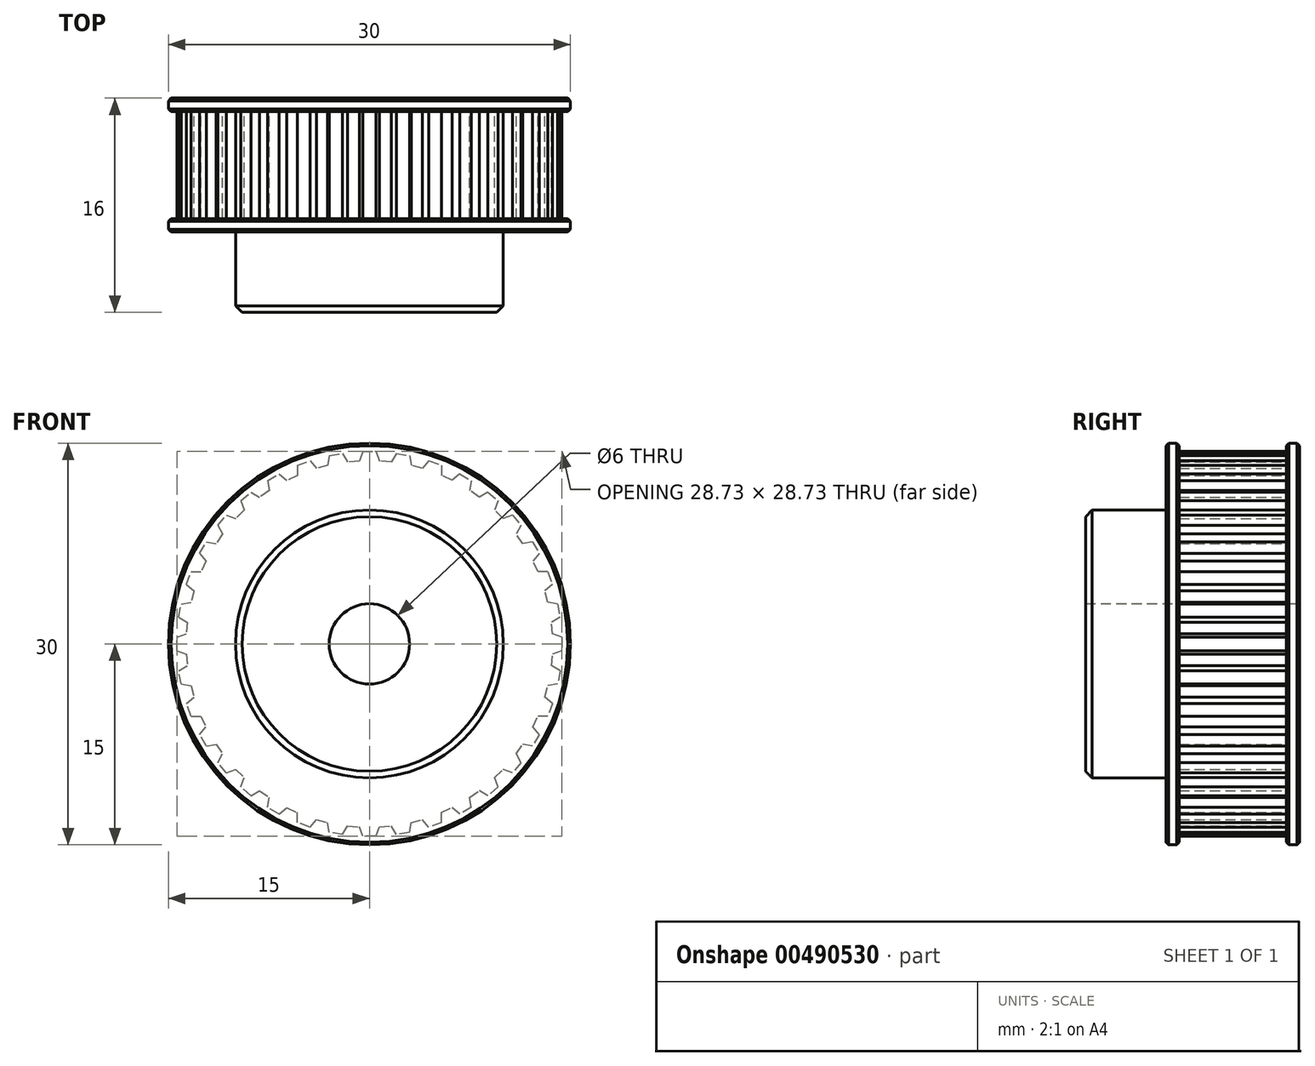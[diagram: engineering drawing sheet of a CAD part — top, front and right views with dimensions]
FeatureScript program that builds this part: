
annotation { "Feature Type Name" : "Feature", "Feature Type Description" : "" }
export const myFeature = defineFeature(function(context is Context, id is Id, definition is map)
    precondition{}
    {
        {
            var Q0;
            Q0=qCreatedBy(makeId("Front.planeOp"),FACE);
            var sketch = newSketch(context, id + "F0", { "sketchPlane" : qUnion([Q0])});
            skCircle(sketch, "E0", {"center": v(0, 0) * mm, "radius": 14.38 * mm, "construction": true});
            skCircle(sketch, "E1", {"center": v(0, 0) * mm, "radius": 10 * mm});
            skLineSegment(sketch, "E2", {"start": v(0, 14.37) * mm, "end": v(-0.5, 14.37) * mm});
            skLineSegment(sketch, "E3", {"start": v(-0.5, 14.37) * mm, "end": v(-0.75, 13.67) * mm});
            skLineSegment(sketch, "E4", {"start": v(-0.75, 13.67) * mm, "end": v(0, 13.67) * mm});
            skLineSegment(sketch, "E5.MirrorCS", {"start": v(0.75, 13.67) * mm, "end": v(0, 13.67) * mm});
            skLineSegment(sketch, "E6.MirrorCS", {"start": v(0, 14.37) * mm, "end": v(0.5, 14.37) * mm});
            skLineSegment(sketch, "E7.MirrorCS", {"start": v(0.5, 14.37) * mm, "end": v(0.75, 13.67) * mm});
            skLineSegment(sketch, "E8.1.0", {"start": v(1.63, 13.59) * mm, "end": v(2.37, 13.46) * mm});
            skLineSegment(sketch, "E8.1.1", {"start": v(3.12, 13.33) * mm, "end": v(2.37, 13.46) * mm});
            skLineSegment(sketch, "E8.1.2", {"start": v(2.99, 14.06) * mm, "end": v(3.12, 13.33) * mm});
            skLineSegment(sketch, "E8.1.3", {"start": v(2, 14.23) * mm, "end": v(1.63, 13.59) * mm});
            skLineSegment(sketch, "E8.1.4", {"start": v(2.5, 14.15) * mm, "end": v(2.99, 14.06) * mm});
            skLineSegment(sketch, "E8.1.5", {"start": v(2.5, 14.15) * mm, "end": v(2, 14.23) * mm});
            skLineSegment(sketch, "E8.2.0", {"start": v(3.96, 13.1) * mm, "end": v(4.67, 12.84) * mm});
            skLineSegment(sketch, "E8.2.1", {"start": v(5.38, 12.58) * mm, "end": v(4.67, 12.84) * mm});
            skLineSegment(sketch, "E8.2.2", {"start": v(5.38, 13.33) * mm, "end": v(5.38, 12.58) * mm});
            skLineSegment(sketch, "E8.2.3", {"start": v(4.44, 13.67) * mm, "end": v(3.96, 13.1) * mm});
            skLineSegment(sketch, "E8.2.4", {"start": v(4.91, 13.5) * mm, "end": v(5.38, 13.33) * mm});
            skLineSegment(sketch, "E8.2.5", {"start": v(4.91, 13.5) * mm, "end": v(4.44, 13.67) * mm});
            skLineSegment(sketch, "E8.3.0", {"start": v(6.18, 12.21) * mm, "end": v(6.83, 11.84) * mm});
            skLineSegment(sketch, "E8.3.1", {"start": v(7.49, 11.46) * mm, "end": v(6.83, 11.84) * mm});
            skLineSegment(sketch, "E8.3.2", {"start": v(7.62, 12.2) * mm, "end": v(7.49, 11.46) * mm});
            skLineSegment(sketch, "E8.3.3", {"start": v(6.75, 12.7) * mm, "end": v(6.18, 12.21) * mm});
            skLineSegment(sketch, "E8.3.4", {"start": v(7.18, 12.44) * mm, "end": v(7.62, 12.2) * mm});
            skLineSegment(sketch, "E8.3.5", {"start": v(7.18, 12.44) * mm, "end": v(6.75, 12.7) * mm});
            skLineSegment(sketch, "E8.4.0", {"start": v(8.2, 10.95) * mm, "end": v(8.78, 10.47) * mm});
            skLineSegment(sketch, "E8.4.1", {"start": v(9.36, 9.98) * mm, "end": v(8.78, 10.47) * mm});
            skLineSegment(sketch, "E8.4.2", {"start": v(9.62, 10.68) * mm, "end": v(9.36, 9.98) * mm});
            skLineSegment(sketch, "E8.4.3", {"start": v(8.85, 11.33) * mm, "end": v(8.2, 10.95) * mm});
            skLineSegment(sketch, "E8.4.4", {"start": v(9.23, 11) * mm, "end": v(9.62, 10.68) * mm});
            skLineSegment(sketch, "E8.4.5", {"start": v(9.23, 11) * mm, "end": v(8.85, 11.33) * mm});
            skLineSegment(sketch, "E8.5.0", {"start": v(9.98, 9.36) * mm, "end": v(10.47, 8.78) * mm});
            skLineSegment(sketch, "E8.5.1", {"start": v(10.95, 8.2) * mm, "end": v(10.47, 8.78) * mm});
            skLineSegment(sketch, "E8.5.2", {"start": v(11.33, 8.85) * mm, "end": v(10.95, 8.2) * mm});
            skLineSegment(sketch, "E8.5.3", {"start": v(10.68, 9.62) * mm, "end": v(9.98, 9.36) * mm});
            skLineSegment(sketch, "E8.5.4", {"start": v(11, 9.23) * mm, "end": v(11.33, 8.85) * mm});
            skLineSegment(sketch, "E8.5.5", {"start": v(11, 9.23) * mm, "end": v(10.68, 9.62) * mm});
            skLineSegment(sketch, "E8.6.0", {"start": v(11.46, 7.49) * mm, "end": v(11.84, 6.83) * mm});
            skLineSegment(sketch, "E8.6.1", {"start": v(12.21, 6.18) * mm, "end": v(11.84, 6.83) * mm});
            skLineSegment(sketch, "E8.6.2", {"start": v(12.7, 6.75) * mm, "end": v(12.21, 6.18) * mm});
            skLineSegment(sketch, "E8.6.3", {"start": v(12.2, 7.62) * mm, "end": v(11.46, 7.49) * mm});
            skLineSegment(sketch, "E8.6.4", {"start": v(12.44, 7.18) * mm, "end": v(12.7, 6.75) * mm});
            skLineSegment(sketch, "E8.6.5", {"start": v(12.44, 7.18) * mm, "end": v(12.2, 7.62) * mm});
            skLineSegment(sketch, "E8.7.0", {"start": v(12.58, 5.38) * mm, "end": v(12.84, 4.67) * mm});
            skLineSegment(sketch, "E8.7.1", {"start": v(13.1, 3.96) * mm, "end": v(12.84, 4.67) * mm});
            skLineSegment(sketch, "E8.7.2", {"start": v(13.67, 4.44) * mm, "end": v(13.1, 3.96) * mm});
            skLineSegment(sketch, "E8.7.3", {"start": v(13.33, 5.38) * mm, "end": v(12.58, 5.38) * mm});
            skLineSegment(sketch, "E8.7.4", {"start": v(13.5, 4.91) * mm, "end": v(13.67, 4.44) * mm});
            skLineSegment(sketch, "E8.7.5", {"start": v(13.5, 4.91) * mm, "end": v(13.33, 5.38) * mm});
            skLineSegment(sketch, "E8.8.0", {"start": v(13.33, 3.12) * mm, "end": v(13.46, 2.37) * mm});
            skLineSegment(sketch, "E8.8.1", {"start": v(13.59, 1.63) * mm, "end": v(13.46, 2.37) * mm});
            skLineSegment(sketch, "E8.8.2", {"start": v(14.23, 2) * mm, "end": v(13.59, 1.63) * mm});
            skLineSegment(sketch, "E8.8.3", {"start": v(14.06, 2.99) * mm, "end": v(13.33, 3.12) * mm});
            skLineSegment(sketch, "E8.8.4", {"start": v(14.15, 2.5) * mm, "end": v(14.23, 2) * mm});
            skLineSegment(sketch, "E8.8.5", {"start": v(14.15, 2.5) * mm, "end": v(14.06, 2.99) * mm});
            skLineSegment(sketch, "E8.9.0", {"start": v(13.67, 0.75) * mm, "end": v(13.67, 0) * mm});
            skLineSegment(sketch, "E8.9.1", {"start": v(13.67, -0.75) * mm, "end": v(13.67, 0) * mm});
            skLineSegment(sketch, "E8.9.2", {"start": v(14.37, -0.5) * mm, "end": v(13.67, -0.75) * mm});
            skLineSegment(sketch, "E8.9.3", {"start": v(14.37, 0.5) * mm, "end": v(13.67, 0.75) * mm});
            skLineSegment(sketch, "E8.9.4", {"start": v(14.37, 0) * mm, "end": v(14.37, -0.5) * mm});
            skLineSegment(sketch, "E8.9.5", {"start": v(14.37, 0) * mm, "end": v(14.37, 0.5) * mm});
            skLineSegment(sketch, "E8.10.0", {"start": v(13.59, -1.63) * mm, "end": v(13.46, -2.37) * mm});
            skLineSegment(sketch, "E8.10.1", {"start": v(13.33, -3.12) * mm, "end": v(13.46, -2.37) * mm});
            skLineSegment(sketch, "E8.10.2", {"start": v(14.06, -2.99) * mm, "end": v(13.33, -3.12) * mm});
            skLineSegment(sketch, "E8.10.3", {"start": v(14.23, -2) * mm, "end": v(13.59, -1.63) * mm});
            skLineSegment(sketch, "E8.10.4", {"start": v(14.15, -2.5) * mm, "end": v(14.06, -2.99) * mm});
            skLineSegment(sketch, "E8.10.5", {"start": v(14.15, -2.5) * mm, "end": v(14.23, -2) * mm});
            skLineSegment(sketch, "E8.11.0", {"start": v(13.1, -3.96) * mm, "end": v(12.84, -4.67) * mm});
            skLineSegment(sketch, "E8.11.1", {"start": v(12.58, -5.38) * mm, "end": v(12.84, -4.67) * mm});
            skLineSegment(sketch, "E8.11.2", {"start": v(13.33, -5.38) * mm, "end": v(12.58, -5.38) * mm});
            skLineSegment(sketch, "E8.11.3", {"start": v(13.67, -4.44) * mm, "end": v(13.1, -3.96) * mm});
            skLineSegment(sketch, "E8.11.4", {"start": v(13.5, -4.91) * mm, "end": v(13.33, -5.38) * mm});
            skLineSegment(sketch, "E8.11.5", {"start": v(13.5, -4.91) * mm, "end": v(13.67, -4.44) * mm});
            skLineSegment(sketch, "E8.12.0", {"start": v(12.21, -6.18) * mm, "end": v(11.84, -6.83) * mm});
            skLineSegment(sketch, "E8.12.1", {"start": v(11.46, -7.49) * mm, "end": v(11.84, -6.83) * mm});
            skLineSegment(sketch, "E8.12.2", {"start": v(12.2, -7.62) * mm, "end": v(11.46, -7.49) * mm});
            skLineSegment(sketch, "E8.12.3", {"start": v(12.7, -6.75) * mm, "end": v(12.21, -6.18) * mm});
            skLineSegment(sketch, "E8.12.4", {"start": v(12.44, -7.18) * mm, "end": v(12.2, -7.62) * mm});
            skLineSegment(sketch, "E8.12.5", {"start": v(12.44, -7.18) * mm, "end": v(12.7, -6.75) * mm});
            skLineSegment(sketch, "E8.13.0", {"start": v(10.95, -8.2) * mm, "end": v(10.47, -8.78) * mm});
            skLineSegment(sketch, "E8.13.1", {"start": v(9.98, -9.36) * mm, "end": v(10.47, -8.78) * mm});
            skLineSegment(sketch, "E8.13.2", {"start": v(10.68, -9.62) * mm, "end": v(9.98, -9.36) * mm});
            skLineSegment(sketch, "E8.13.3", {"start": v(11.33, -8.85) * mm, "end": v(10.95, -8.2) * mm});
            skLineSegment(sketch, "E8.13.4", {"start": v(11, -9.23) * mm, "end": v(10.68, -9.62) * mm});
            skLineSegment(sketch, "E8.13.5", {"start": v(11, -9.23) * mm, "end": v(11.33, -8.85) * mm});
            skLineSegment(sketch, "E8.14.0", {"start": v(9.36, -9.98) * mm, "end": v(8.78, -10.47) * mm});
            skLineSegment(sketch, "E8.14.1", {"start": v(8.2, -10.95) * mm, "end": v(8.78, -10.47) * mm});
            skLineSegment(sketch, "E8.14.2", {"start": v(8.85, -11.33) * mm, "end": v(8.2, -10.95) * mm});
            skLineSegment(sketch, "E8.14.3", {"start": v(9.62, -10.68) * mm, "end": v(9.36, -9.98) * mm});
            skLineSegment(sketch, "E8.14.4", {"start": v(9.23, -11) * mm, "end": v(8.85, -11.33) * mm});
            skLineSegment(sketch, "E8.14.5", {"start": v(9.23, -11) * mm, "end": v(9.62, -10.68) * mm});
            skLineSegment(sketch, "E8.15.0", {"start": v(7.49, -11.46) * mm, "end": v(6.83, -11.84) * mm});
            skLineSegment(sketch, "E8.15.1", {"start": v(6.18, -12.21) * mm, "end": v(6.83, -11.84) * mm});
            skLineSegment(sketch, "E8.15.2", {"start": v(6.75, -12.7) * mm, "end": v(6.18, -12.21) * mm});
            skLineSegment(sketch, "E8.15.3", {"start": v(7.62, -12.2) * mm, "end": v(7.49, -11.46) * mm});
            skLineSegment(sketch, "E8.15.4", {"start": v(7.18, -12.44) * mm, "end": v(6.75, -12.7) * mm});
            skLineSegment(sketch, "E8.15.5", {"start": v(7.18, -12.44) * mm, "end": v(7.62, -12.2) * mm});
            skLineSegment(sketch, "E8.16.0", {"start": v(5.38, -12.58) * mm, "end": v(4.67, -12.84) * mm});
            skLineSegment(sketch, "E8.16.1", {"start": v(3.96, -13.1) * mm, "end": v(4.67, -12.84) * mm});
            skLineSegment(sketch, "E8.16.2", {"start": v(4.44, -13.67) * mm, "end": v(3.96, -13.1) * mm});
            skLineSegment(sketch, "E8.16.3", {"start": v(5.38, -13.33) * mm, "end": v(5.38, -12.58) * mm});
            skLineSegment(sketch, "E8.16.4", {"start": v(4.91, -13.5) * mm, "end": v(4.44, -13.67) * mm});
            skLineSegment(sketch, "E8.16.5", {"start": v(4.91, -13.5) * mm, "end": v(5.38, -13.33) * mm});
            skLineSegment(sketch, "E8.17.0", {"start": v(3.12, -13.33) * mm, "end": v(2.37, -13.46) * mm});
            skLineSegment(sketch, "E8.17.1", {"start": v(1.63, -13.59) * mm, "end": v(2.37, -13.46) * mm});
            skLineSegment(sketch, "E8.17.2", {"start": v(2, -14.23) * mm, "end": v(1.63, -13.59) * mm});
            skLineSegment(sketch, "E8.17.3", {"start": v(2.99, -14.06) * mm, "end": v(3.12, -13.33) * mm});
            skLineSegment(sketch, "E8.17.4", {"start": v(2.5, -14.15) * mm, "end": v(2, -14.23) * mm});
            skLineSegment(sketch, "E8.17.5", {"start": v(2.5, -14.15) * mm, "end": v(2.99, -14.06) * mm});
            skLineSegment(sketch, "E8.18.0", {"start": v(0.75, -13.67) * mm, "end": v(0, -13.67) * mm});
            skLineSegment(sketch, "E8.18.1", {"start": v(-0.75, -13.67) * mm, "end": v(0, -13.67) * mm});
            skLineSegment(sketch, "E8.18.2", {"start": v(-0.5, -14.37) * mm, "end": v(-0.75, -13.67) * mm});
            skLineSegment(sketch, "E8.18.3", {"start": v(0.5, -14.37) * mm, "end": v(0.75, -13.67) * mm});
            skLineSegment(sketch, "E8.18.4", {"start": v(0, -14.37) * mm, "end": v(-0.5, -14.37) * mm});
            skLineSegment(sketch, "E8.18.5", {"start": v(0, -14.37) * mm, "end": v(0.5, -14.37) * mm});
            skLineSegment(sketch, "E8.19.0", {"start": v(-1.63, -13.59) * mm, "end": v(-2.37, -13.46) * mm});
            skLineSegment(sketch, "E8.19.1", {"start": v(-3.12, -13.33) * mm, "end": v(-2.37, -13.46) * mm});
            skLineSegment(sketch, "E8.19.2", {"start": v(-2.99, -14.06) * mm, "end": v(-3.12, -13.33) * mm});
            skLineSegment(sketch, "E8.19.3", {"start": v(-2, -14.23) * mm, "end": v(-1.63, -13.59) * mm});
            skLineSegment(sketch, "E8.19.4", {"start": v(-2.5, -14.15) * mm, "end": v(-2.99, -14.06) * mm});
            skLineSegment(sketch, "E8.19.5", {"start": v(-2.5, -14.15) * mm, "end": v(-2, -14.23) * mm});
            skLineSegment(sketch, "E8.20.0", {"start": v(-3.96, -13.1) * mm, "end": v(-4.67, -12.84) * mm});
            skLineSegment(sketch, "E8.20.1", {"start": v(-5.38, -12.58) * mm, "end": v(-4.67, -12.84) * mm});
            skLineSegment(sketch, "E8.20.2", {"start": v(-5.38, -13.33) * mm, "end": v(-5.38, -12.58) * mm});
            skLineSegment(sketch, "E8.20.3", {"start": v(-4.44, -13.67) * mm, "end": v(-3.96, -13.1) * mm});
            skLineSegment(sketch, "E8.20.4", {"start": v(-4.91, -13.5) * mm, "end": v(-5.38, -13.33) * mm});
            skLineSegment(sketch, "E8.20.5", {"start": v(-4.91, -13.5) * mm, "end": v(-4.44, -13.67) * mm});
            skLineSegment(sketch, "E8.21.0", {"start": v(-6.18, -12.21) * mm, "end": v(-6.83, -11.84) * mm});
            skLineSegment(sketch, "E8.21.1", {"start": v(-7.49, -11.46) * mm, "end": v(-6.83, -11.84) * mm});
            skLineSegment(sketch, "E8.21.2", {"start": v(-7.62, -12.2) * mm, "end": v(-7.49, -11.46) * mm});
            skLineSegment(sketch, "E8.21.3", {"start": v(-6.75, -12.7) * mm, "end": v(-6.18, -12.21) * mm});
            skLineSegment(sketch, "E8.21.4", {"start": v(-7.18, -12.44) * mm, "end": v(-7.62, -12.2) * mm});
            skLineSegment(sketch, "E8.21.5", {"start": v(-7.18, -12.44) * mm, "end": v(-6.75, -12.7) * mm});
            skLineSegment(sketch, "E8.22.0", {"start": v(-8.2, -10.95) * mm, "end": v(-8.78, -10.47) * mm});
            skLineSegment(sketch, "E8.22.1", {"start": v(-9.36, -9.98) * mm, "end": v(-8.78, -10.47) * mm});
            skLineSegment(sketch, "E8.22.2", {"start": v(-9.62, -10.68) * mm, "end": v(-9.36, -9.98) * mm});
            skLineSegment(sketch, "E8.22.3", {"start": v(-8.85, -11.33) * mm, "end": v(-8.2, -10.95) * mm});
            skLineSegment(sketch, "E8.22.4", {"start": v(-9.23, -11) * mm, "end": v(-9.62, -10.68) * mm});
            skLineSegment(sketch, "E8.22.5", {"start": v(-9.23, -11) * mm, "end": v(-8.85, -11.33) * mm});
            skLineSegment(sketch, "E8.23.0", {"start": v(-9.98, -9.36) * mm, "end": v(-10.47, -8.78) * mm});
            skLineSegment(sketch, "E8.23.1", {"start": v(-10.95, -8.2) * mm, "end": v(-10.47, -8.78) * mm});
            skLineSegment(sketch, "E8.23.2", {"start": v(-11.33, -8.85) * mm, "end": v(-10.95, -8.2) * mm});
            skLineSegment(sketch, "E8.23.3", {"start": v(-10.68, -9.62) * mm, "end": v(-9.98, -9.36) * mm});
            skLineSegment(sketch, "E8.23.4", {"start": v(-11, -9.23) * mm, "end": v(-11.33, -8.85) * mm});
            skLineSegment(sketch, "E8.23.5", {"start": v(-11, -9.23) * mm, "end": v(-10.68, -9.62) * mm});
            skLineSegment(sketch, "E8.anchor1", {"start": v(0, 0) * mm, "end": v(-0.75, 13.67) * mm, "construction": true});
            skLineSegment(sketch, "E8.anchor2", {"start": v(0, 0) * mm, "end": v(-3.12, 13.33) * mm, "construction": true});
            skLineSegment(sketch, "E9", {"start": v(-0.75, 13.67) * mm, "end": v(-1.63, 13.59) * mm});
            skLineSegment(sketch, "E10.1.0", {"start": v(1.63, 13.59) * mm, "end": v(0.75, 13.67) * mm});
            skLineSegment(sketch, "E10.2.0", {"start": v(3.96, 13.1) * mm, "end": v(3.12, 13.33) * mm});
            skLineSegment(sketch, "E10.3.0", {"start": v(6.18, 12.21) * mm, "end": v(5.38, 12.58) * mm});
            skLineSegment(sketch, "E10.4.0", {"start": v(8.2, 10.95) * mm, "end": v(7.49, 11.46) * mm});
            skLineSegment(sketch, "E10.5.0", {"start": v(9.98, 9.36) * mm, "end": v(9.36, 9.98) * mm});
            skLineSegment(sketch, "E10.6.0", {"start": v(11.46, 7.49) * mm, "end": v(10.95, 8.2) * mm});
            skLineSegment(sketch, "E10.7.0", {"start": v(12.58, 5.38) * mm, "end": v(12.21, 6.18) * mm});
            skLineSegment(sketch, "E10.8.0", {"start": v(13.33, 3.12) * mm, "end": v(13.1, 3.96) * mm});
            skLineSegment(sketch, "E10.9.0", {"start": v(13.67, 0.75) * mm, "end": v(13.59, 1.63) * mm});
            skLineSegment(sketch, "E10.10.0", {"start": v(13.59, -1.63) * mm, "end": v(13.67, -0.75) * mm});
            skLineSegment(sketch, "E10.11.0", {"start": v(13.1, -3.96) * mm, "end": v(13.33, -3.12) * mm});
            skLineSegment(sketch, "E10.12.0", {"start": v(12.21, -6.18) * mm, "end": v(12.58, -5.38) * mm});
            skLineSegment(sketch, "E10.13.0", {"start": v(10.95, -8.2) * mm, "end": v(11.46, -7.49) * mm});
            skLineSegment(sketch, "E10.14.0", {"start": v(9.36, -9.98) * mm, "end": v(9.98, -9.36) * mm});
            skLineSegment(sketch, "E10.15.0", {"start": v(7.49, -11.46) * mm, "end": v(8.2, -10.95) * mm});
            skLineSegment(sketch, "E10.16.0", {"start": v(5.38, -12.58) * mm, "end": v(6.18, -12.21) * mm});
            skLineSegment(sketch, "E10.17.0", {"start": v(3.12, -13.33) * mm, "end": v(3.96, -13.1) * mm});
            skLineSegment(sketch, "E10.18.0", {"start": v(0.75, -13.67) * mm, "end": v(1.63, -13.59) * mm});
            skLineSegment(sketch, "E10.19.0", {"start": v(-1.63, -13.59) * mm, "end": v(-0.75, -13.67) * mm});
            skLineSegment(sketch, "E10.20.0", {"start": v(-3.96, -13.1) * mm, "end": v(-3.12, -13.33) * mm});
            skLineSegment(sketch, "E10.21.0", {"start": v(-6.18, -12.21) * mm, "end": v(-5.38, -12.58) * mm});
            skLineSegment(sketch, "E10.22.0", {"start": v(-8.2, -10.95) * mm, "end": v(-7.49, -11.46) * mm});
            skLineSegment(sketch, "E10.23.0", {"start": v(-9.98, -9.36) * mm, "end": v(-9.36, -9.98) * mm});
            skLineSegment(sketch, "E10.anchor1", {"start": v(0, 0) * mm, "end": v(-1.63, 13.59) * mm, "construction": true});
            skLineSegment(sketch, "E10.anchor2", {"start": v(0, 0) * mm, "end": v(-3.96, 13.1) * mm, "construction": true});
            skLineSegment(sketch, "E11.2.24.0", {"start": v(-11.46, -7.49) * mm, "end": v(-10.95, -8.2) * mm});
            skLineSegment(sketch, "E11.2.25.0", {"start": v(-12.58, -5.38) * mm, "end": v(-12.21, -6.18) * mm});
            skLineSegment(sketch, "E11.2.26.0", {"start": v(-13.33, -3.12) * mm, "end": v(-13.1, -3.96) * mm});
            skLineSegment(sketch, "E11.2.27.0", {"start": v(-13.67, -0.75) * mm, "end": v(-13.59, -1.63) * mm});
            skLineSegment(sketch, "E11.2.28.0", {"start": v(-13.59, 1.63) * mm, "end": v(-13.67, 0.75) * mm});
            skLineSegment(sketch, "E11.2.29.0", {"start": v(-13.1, 3.96) * mm, "end": v(-13.33, 3.12) * mm});
            skLineSegment(sketch, "E11.2.30.0", {"start": v(-12.21, 6.18) * mm, "end": v(-12.58, 5.38) * mm});
            skLineSegment(sketch, "E11.2.31.0", {"start": v(-10.95, 8.2) * mm, "end": v(-11.46, 7.49) * mm});
            skLineSegment(sketch, "E11.2.32.0", {"start": v(-9.36, 9.98) * mm, "end": v(-9.98, 9.36) * mm});
            skLineSegment(sketch, "E11.2.33.0", {"start": v(-7.49, 11.46) * mm, "end": v(-8.2, 10.95) * mm});
            skLineSegment(sketch, "E11.2.34.0", {"start": v(-5.38, 12.58) * mm, "end": v(-6.18, 12.21) * mm});
            skLineSegment(sketch, "E11.2.35.0", {"start": v(-3.12, 13.33) * mm, "end": v(-3.96, 13.1) * mm});
            skLineSegment(sketch, "E12.1.24.0", {"start": v(-11.46, -7.49) * mm, "end": v(-11.84, -6.83) * mm});
            skLineSegment(sketch, "E12.3.24.0", {"start": v(-12.21, -6.18) * mm, "end": v(-11.84, -6.83) * mm});
            skLineSegment(sketch, "E12.6.24.0", {"start": v(-12.7, -6.75) * mm, "end": v(-12.21, -6.18) * mm});
            skLineSegment(sketch, "E12.9.24.0", {"start": v(-12.2, -7.62) * mm, "end": v(-11.46, -7.49) * mm});
            skLineSegment(sketch, "E12.12.24.0", {"start": v(-12.44, -7.18) * mm, "end": v(-12.7, -6.75) * mm});
            skLineSegment(sketch, "E12.15.24.0", {"start": v(-12.44, -7.18) * mm, "end": v(-12.2, -7.62) * mm});
            skLineSegment(sketch, "E12.1.25.0", {"start": v(-12.58, -5.38) * mm, "end": v(-12.84, -4.67) * mm});
            skLineSegment(sketch, "E12.3.25.0", {"start": v(-13.1, -3.96) * mm, "end": v(-12.84, -4.67) * mm});
            skLineSegment(sketch, "E12.6.25.0", {"start": v(-13.67, -4.44) * mm, "end": v(-13.1, -3.96) * mm});
            skLineSegment(sketch, "E12.9.25.0", {"start": v(-13.33, -5.38) * mm, "end": v(-12.58, -5.38) * mm});
            skLineSegment(sketch, "E12.12.25.0", {"start": v(-13.5, -4.91) * mm, "end": v(-13.67, -4.44) * mm});
            skLineSegment(sketch, "E12.15.25.0", {"start": v(-13.5, -4.91) * mm, "end": v(-13.33, -5.38) * mm});
            skLineSegment(sketch, "E12.1.26.0", {"start": v(-13.33, -3.12) * mm, "end": v(-13.46, -2.37) * mm});
            skLineSegment(sketch, "E12.3.26.0", {"start": v(-13.59, -1.63) * mm, "end": v(-13.46, -2.37) * mm});
            skLineSegment(sketch, "E12.6.26.0", {"start": v(-14.23, -2) * mm, "end": v(-13.59, -1.63) * mm});
            skLineSegment(sketch, "E12.9.26.0", {"start": v(-14.06, -2.99) * mm, "end": v(-13.33, -3.12) * mm});
            skLineSegment(sketch, "E12.12.26.0", {"start": v(-14.15, -2.5) * mm, "end": v(-14.23, -2) * mm});
            skLineSegment(sketch, "E12.15.26.0", {"start": v(-14.15, -2.5) * mm, "end": v(-14.06, -2.99) * mm});
            skLineSegment(sketch, "E12.1.27.0", {"start": v(-13.67, -0.75) * mm, "end": v(-13.67, 0) * mm});
            skLineSegment(sketch, "E12.3.27.0", {"start": v(-13.67, 0.75) * mm, "end": v(-13.67, 0) * mm});
            skLineSegment(sketch, "E12.6.27.0", {"start": v(-14.37, 0.5) * mm, "end": v(-13.67, 0.75) * mm});
            skLineSegment(sketch, "E12.9.27.0", {"start": v(-14.37, -0.5) * mm, "end": v(-13.67, -0.75) * mm});
            skLineSegment(sketch, "E12.12.27.0", {"start": v(-14.37, 0) * mm, "end": v(-14.37, 0.5) * mm});
            skLineSegment(sketch, "E12.15.27.0", {"start": v(-14.37, 0) * mm, "end": v(-14.37, -0.5) * mm});
            skLineSegment(sketch, "E12.1.28.0", {"start": v(-13.59, 1.63) * mm, "end": v(-13.46, 2.37) * mm});
            skLineSegment(sketch, "E12.3.28.0", {"start": v(-13.33, 3.12) * mm, "end": v(-13.46, 2.37) * mm});
            skLineSegment(sketch, "E12.6.28.0", {"start": v(-14.06, 2.99) * mm, "end": v(-13.33, 3.12) * mm});
            skLineSegment(sketch, "E12.9.28.0", {"start": v(-14.23, 2) * mm, "end": v(-13.59, 1.63) * mm});
            skLineSegment(sketch, "E12.12.28.0", {"start": v(-14.15, 2.5) * mm, "end": v(-14.06, 2.99) * mm});
            skLineSegment(sketch, "E12.15.28.0", {"start": v(-14.15, 2.5) * mm, "end": v(-14.23, 2) * mm});
            skLineSegment(sketch, "E12.1.29.0", {"start": v(-13.1, 3.96) * mm, "end": v(-12.84, 4.67) * mm});
            skLineSegment(sketch, "E12.3.29.0", {"start": v(-12.58, 5.38) * mm, "end": v(-12.84, 4.67) * mm});
            skLineSegment(sketch, "E12.6.29.0", {"start": v(-13.33, 5.38) * mm, "end": v(-12.58, 5.38) * mm});
            skLineSegment(sketch, "E12.9.29.0", {"start": v(-13.67, 4.44) * mm, "end": v(-13.1, 3.96) * mm});
            skLineSegment(sketch, "E12.12.29.0", {"start": v(-13.5, 4.91) * mm, "end": v(-13.33, 5.38) * mm});
            skLineSegment(sketch, "E12.15.29.0", {"start": v(-13.5, 4.91) * mm, "end": v(-13.67, 4.44) * mm});
            skLineSegment(sketch, "E12.1.30.0", {"start": v(-12.21, 6.18) * mm, "end": v(-11.84, 6.83) * mm});
            skLineSegment(sketch, "E12.3.30.0", {"start": v(-11.46, 7.49) * mm, "end": v(-11.84, 6.83) * mm});
            skLineSegment(sketch, "E12.6.30.0", {"start": v(-12.2, 7.62) * mm, "end": v(-11.46, 7.49) * mm});
            skLineSegment(sketch, "E12.9.30.0", {"start": v(-12.7, 6.75) * mm, "end": v(-12.21, 6.18) * mm});
            skLineSegment(sketch, "E12.12.30.0", {"start": v(-12.44, 7.18) * mm, "end": v(-12.2, 7.62) * mm});
            skLineSegment(sketch, "E12.15.30.0", {"start": v(-12.44, 7.18) * mm, "end": v(-12.7, 6.75) * mm});
            skLineSegment(sketch, "E12.1.31.0", {"start": v(-10.95, 8.2) * mm, "end": v(-10.47, 8.78) * mm});
            skLineSegment(sketch, "E12.3.31.0", {"start": v(-9.98, 9.36) * mm, "end": v(-10.47, 8.78) * mm});
            skLineSegment(sketch, "E12.6.31.0", {"start": v(-10.68, 9.62) * mm, "end": v(-9.98, 9.36) * mm});
            skLineSegment(sketch, "E12.9.31.0", {"start": v(-11.33, 8.85) * mm, "end": v(-10.95, 8.2) * mm});
            skLineSegment(sketch, "E12.12.31.0", {"start": v(-11, 9.23) * mm, "end": v(-10.68, 9.62) * mm});
            skLineSegment(sketch, "E12.15.31.0", {"start": v(-11, 9.23) * mm, "end": v(-11.33, 8.85) * mm});
            skLineSegment(sketch, "E12.1.32.0", {"start": v(-9.36, 9.98) * mm, "end": v(-8.78, 10.47) * mm});
            skLineSegment(sketch, "E12.3.32.0", {"start": v(-8.2, 10.95) * mm, "end": v(-8.78, 10.47) * mm});
            skLineSegment(sketch, "E12.6.32.0", {"start": v(-8.85, 11.33) * mm, "end": v(-8.2, 10.95) * mm});
            skLineSegment(sketch, "E12.9.32.0", {"start": v(-9.62, 10.68) * mm, "end": v(-9.36, 9.98) * mm});
            skLineSegment(sketch, "E12.12.32.0", {"start": v(-9.23, 11) * mm, "end": v(-8.85, 11.33) * mm});
            skLineSegment(sketch, "E12.15.32.0", {"start": v(-9.23, 11) * mm, "end": v(-9.62, 10.68) * mm});
            skLineSegment(sketch, "E12.1.33.0", {"start": v(-7.49, 11.46) * mm, "end": v(-6.83, 11.84) * mm});
            skLineSegment(sketch, "E12.3.33.0", {"start": v(-6.18, 12.21) * mm, "end": v(-6.83, 11.84) * mm});
            skLineSegment(sketch, "E12.6.33.0", {"start": v(-6.75, 12.7) * mm, "end": v(-6.18, 12.21) * mm});
            skLineSegment(sketch, "E12.9.33.0", {"start": v(-7.62, 12.2) * mm, "end": v(-7.49, 11.46) * mm});
            skLineSegment(sketch, "E12.12.33.0", {"start": v(-7.18, 12.44) * mm, "end": v(-6.75, 12.7) * mm});
            skLineSegment(sketch, "E12.15.33.0", {"start": v(-7.18, 12.44) * mm, "end": v(-7.62, 12.2) * mm});
            skLineSegment(sketch, "E12.1.34.0", {"start": v(-5.38, 12.58) * mm, "end": v(-4.67, 12.84) * mm});
            skLineSegment(sketch, "E12.3.34.0", {"start": v(-3.96, 13.1) * mm, "end": v(-4.67, 12.84) * mm});
            skLineSegment(sketch, "E12.6.34.0", {"start": v(-4.44, 13.67) * mm, "end": v(-3.96, 13.1) * mm});
            skLineSegment(sketch, "E12.9.34.0", {"start": v(-5.38, 13.33) * mm, "end": v(-5.38, 12.58) * mm});
            skLineSegment(sketch, "E12.12.34.0", {"start": v(-4.91, 13.5) * mm, "end": v(-4.44, 13.67) * mm});
            skLineSegment(sketch, "E12.15.34.0", {"start": v(-4.91, 13.5) * mm, "end": v(-5.38, 13.33) * mm});
            skLineSegment(sketch, "E12.1.35.0", {"start": v(-3.12, 13.33) * mm, "end": v(-2.37, 13.46) * mm});
            skLineSegment(sketch, "E12.3.35.0", {"start": v(-1.63, 13.59) * mm, "end": v(-2.37, 13.46) * mm});
            skLineSegment(sketch, "E12.6.35.0", {"start": v(-2, 14.23) * mm, "end": v(-1.63, 13.59) * mm});
            skLineSegment(sketch, "E12.9.35.0", {"start": v(-2.99, 14.06) * mm, "end": v(-3.12, 13.33) * mm});
            skLineSegment(sketch, "E12.12.35.0", {"start": v(-2.5, 14.15) * mm, "end": v(-2, 14.23) * mm});
            skLineSegment(sketch, "E12.15.35.0", {"start": v(-2.5, 14.15) * mm, "end": v(-2.99, 14.06) * mm});
            skSolve(sketch);
        }
        {
            var Q0;
            Q0 = qSketchRegion(id + "F0", true);
            extrude(context, id + "F1", {"entities" : qUnion([Q0]), "depth" : 10 * mm});
        }
        {
            var Q0;
            Q0=makeQuery(id+"F0.imprint","IMPRINT",FACE,{"disambiguationData":[TD([[makeQuery(id+"F0.imprint","IMPRINT",EDGE,{"derivedFrom":sQuery(id+"F0.wireOp",EDGE,"E1")}),-1.0]])]});
            var sketch = newSketch(context, id + "F2", { "sketchPlane" : qUnion([Q0])});
            skCircle(sketch, "E13", {"center": v(0, 0) * mm, "radius": 15 * mm});
            skSolve(sketch);
        }
        {
            var Q0;
            Q0=makeQuery(id+"F1.opExtrude","CAP_FACE",FACE,{"disambiguationData":[OSD([sQuery(id+"F0.wireOp",EDGE,"E1"),sQuery(id+"F0.wireOp",EDGE,"E2"),sQuery(id+"F0.wireOp",EDGE,"E3"),sQuery(id+"F0.wireOp",EDGE,"E6.MirrorCS"),sQuery(id+"F0.wireOp",EDGE,"E7.MirrorCS"),sQuery(id+"F0.wireOp",EDGE,"E8.1.2"),sQuery(id+"F0.wireOp",EDGE,"E8.1.3"),sQuery(id+"F0.wireOp",EDGE,"E8.1.4"),sQuery(id+"F0.wireOp",EDGE,"E8.1.5"),sQuery(id+"F0.wireOp",EDGE,"E8.2.2"),sQuery(id+"F0.wireOp",EDGE,"E8.2.3"),sQuery(id+"F0.wireOp",EDGE,"E8.2.4"),sQuery(id+"F0.wireOp",EDGE,"E8.2.5"),sQuery(id+"F0.wireOp",EDGE,"E8.3.2"),sQuery(id+"F0.wireOp",EDGE,"E8.3.3"),sQuery(id+"F0.wireOp",EDGE,"E8.3.4"),sQuery(id+"F0.wireOp",EDGE,"E8.3.5"),sQuery(id+"F0.wireOp",EDGE,"E8.4.2"),sQuery(id+"F0.wireOp",EDGE,"E8.4.3"),sQuery(id+"F0.wireOp",EDGE,"E8.4.4"),sQuery(id+"F0.wireOp",EDGE,"E8.4.5"),sQuery(id+"F0.wireOp",EDGE,"E8.5.2"),sQuery(id+"F0.wireOp",EDGE,"E8.5.3"),sQuery(id+"F0.wireOp",EDGE,"E8.5.4"),sQuery(id+"F0.wireOp",EDGE,"E8.5.5"),sQuery(id+"F0.wireOp",EDGE,"E8.6.2"),sQuery(id+"F0.wireOp",EDGE,"E8.6.3"),sQuery(id+"F0.wireOp",EDGE,"E8.6.4"),sQuery(id+"F0.wireOp",EDGE,"E8.6.5"),sQuery(id+"F0.wireOp",EDGE,"E8.7.2"),sQuery(id+"F0.wireOp",EDGE,"E8.7.3"),sQuery(id+"F0.wireOp",EDGE,"E8.7.4"),sQuery(id+"F0.wireOp",EDGE,"E8.7.5"),sQuery(id+"F0.wireOp",EDGE,"E8.8.2"),sQuery(id+"F0.wireOp",EDGE,"E8.8.3"),sQuery(id+"F0.wireOp",EDGE,"E8.8.4"),sQuery(id+"F0.wireOp",EDGE,"E8.8.5"),sQuery(id+"F0.wireOp",EDGE,"E8.9.2"),sQuery(id+"F0.wireOp",EDGE,"E8.9.3"),sQuery(id+"F0.wireOp",EDGE,"E8.9.4"),sQuery(id+"F0.wireOp",EDGE,"E8.9.5"),sQuery(id+"F0.wireOp",EDGE,"E8.10.2"),sQuery(id+"F0.wireOp",EDGE,"E8.10.3"),sQuery(id+"F0.wireOp",EDGE,"E8.10.4"),sQuery(id+"F0.wireOp",EDGE,"E8.10.5"),sQuery(id+"F0.wireOp",EDGE,"E8.11.2"),sQuery(id+"F0.wireOp",EDGE,"E8.11.3"),sQuery(id+"F0.wireOp",EDGE,"E8.11.4"),sQuery(id+"F0.wireOp",EDGE,"E8.11.5"),sQuery(id+"F0.wireOp",EDGE,"E8.12.2"),sQuery(id+"F0.wireOp",EDGE,"E8.12.3"),sQuery(id+"F0.wireOp",EDGE,"E8.12.4"),sQuery(id+"F0.wireOp",EDGE,"E8.12.5"),sQuery(id+"F0.wireOp",EDGE,"E8.13.2"),sQuery(id+"F0.wireOp",EDGE,"E8.13.3"),sQuery(id+"F0.wireOp",EDGE,"E8.13.4"),sQuery(id+"F0.wireOp",EDGE,"E8.13.5"),sQuery(id+"F0.wireOp",EDGE,"E8.14.2"),sQuery(id+"F0.wireOp",EDGE,"E8.14.3"),sQuery(id+"F0.wireOp",EDGE,"E8.14.4"),sQuery(id+"F0.wireOp",EDGE,"E8.14.5"),sQuery(id+"F0.wireOp",EDGE,"E8.15.2"),sQuery(id+"F0.wireOp",EDGE,"E8.15.3"),sQuery(id+"F0.wireOp",EDGE,"E8.15.4"),sQuery(id+"F0.wireOp",EDGE,"E8.15.5"),sQuery(id+"F0.wireOp",EDGE,"E8.16.2"),sQuery(id+"F0.wireOp",EDGE,"E8.16.3"),sQuery(id+"F0.wireOp",EDGE,"E8.16.4"),sQuery(id+"F0.wireOp",EDGE,"E8.16.5"),sQuery(id+"F0.wireOp",EDGE,"E8.17.2"),sQuery(id+"F0.wireOp",EDGE,"E8.17.3"),sQuery(id+"F0.wireOp",EDGE,"E8.17.4"),sQuery(id+"F0.wireOp",EDGE,"E8.17.5"),sQuery(id+"F0.wireOp",EDGE,"E8.18.2"),sQuery(id+"F0.wireOp",EDGE,"E8.18.3"),sQuery(id+"F0.wireOp",EDGE,"E8.18.4"),sQuery(id+"F0.wireOp",EDGE,"E8.18.5"),sQuery(id+"F0.wireOp",EDGE,"E8.19.2"),sQuery(id+"F0.wireOp",EDGE,"E8.19.3"),sQuery(id+"F0.wireOp",EDGE,"E8.19.4"),sQuery(id+"F0.wireOp",EDGE,"E8.19.5"),sQuery(id+"F0.wireOp",EDGE,"E8.20.2"),sQuery(id+"F0.wireOp",EDGE,"E8.20.3"),sQuery(id+"F0.wireOp",EDGE,"E8.20.4"),sQuery(id+"F0.wireOp",EDGE,"E8.20.5"),sQuery(id+"F0.wireOp",EDGE,"E8.21.2"),sQuery(id+"F0.wireOp",EDGE,"E8.21.3"),sQuery(id+"F0.wireOp",EDGE,"E8.21.4"),sQuery(id+"F0.wireOp",EDGE,"E8.21.5"),sQuery(id+"F0.wireOp",EDGE,"E8.22.2"),sQuery(id+"F0.wireOp",EDGE,"E8.22.3"),sQuery(id+"F0.wireOp",EDGE,"E8.22.4"),sQuery(id+"F0.wireOp",EDGE,"E8.22.5"),sQuery(id+"F0.wireOp",EDGE,"E8.23.2"),sQuery(id+"F0.wireOp",EDGE,"E8.23.3"),sQuery(id+"F0.wireOp",EDGE,"E8.23.4"),sQuery(id+"F0.wireOp",EDGE,"E8.23.5"),sQuery(id+"F0.wireOp",EDGE,"E9"),sQuery(id+"F0.wireOp",EDGE,"E10.1.0"),sQuery(id+"F0.wireOp",EDGE,"E10.2.0"),sQuery(id+"F0.wireOp",EDGE,"E10.3.0"),sQuery(id+"F0.wireOp",EDGE,"E10.4.0"),sQuery(id+"F0.wireOp",EDGE,"E10.5.0"),sQuery(id+"F0.wireOp",EDGE,"E10.6.0"),sQuery(id+"F0.wireOp",EDGE,"E10.7.0"),sQuery(id+"F0.wireOp",EDGE,"E10.8.0"),sQuery(id+"F0.wireOp",EDGE,"E10.9.0"),sQuery(id+"F0.wireOp",EDGE,"E10.10.0"),sQuery(id+"F0.wireOp",EDGE,"E10.11.0"),sQuery(id+"F0.wireOp",EDGE,"E10.12.0"),sQuery(id+"F0.wireOp",EDGE,"E10.13.0"),sQuery(id+"F0.wireOp",EDGE,"E10.14.0"),sQuery(id+"F0.wireOp",EDGE,"E10.15.0"),sQuery(id+"F0.wireOp",EDGE,"E10.16.0"),sQuery(id+"F0.wireOp",EDGE,"E10.17.0"),sQuery(id+"F0.wireOp",EDGE,"E10.18.0"),sQuery(id+"F0.wireOp",EDGE,"E10.19.0"),sQuery(id+"F0.wireOp",EDGE,"E10.20.0"),sQuery(id+"F0.wireOp",EDGE,"E10.21.0"),sQuery(id+"F0.wireOp",EDGE,"E10.22.0"),sQuery(id+"F0.wireOp",EDGE,"E10.23.0")])],"isStart":false});
            var sketch = newSketch(context, id + "F3", { "sketchPlane" : qUnion([Q0])});
            skCircle(sketch, "E14", {"center": v(0, 0) * mm, "radius": 15 * mm});
            skSolve(sketch);
        }
        {
            var Q0;
            Q0=makeQuery(id+"F2.imprint","IMPRINT",FACE,{"disambiguationData":[TD([[makeQuery(id+"F2.imprint","IMPRINT",EDGE,{"derivedFrom":sQuery(id+"F2.wireOp",EDGE,"E13")}),1.0]])]});
            extrude(context, id + "F4", {"entities" : qUnion([Q0]), "operationType" : NewBodyOperationType.ADD, "depth" : 1 * mm});
        }
        {
            var Q0;
            Q0=makeQuery(id+"F3.imprint","IMPRINT",FACE,{"disambiguationData":[TD([[makeQuery(id+"F3.imprint","IMPRINT",EDGE,{"derivedFrom":sQuery(id+"F3.wireOp",EDGE,"E14")}),1.0]])]});
            extrude(context, id + "F5", {"entities" : qUnion([Q0]), "operationType" : NewBodyOperationType.ADD, "oppositeDirection" : true, "depth" : 1 * mm});
        }
        {
            var Q0;
            Q0=makeQuery(id+"F0.imprint","IMPRINT",FACE,{"disambiguationData":[TD([[makeQuery(id+"F0.imprint","IMPRINT",EDGE,{"derivedFrom":sQuery(id+"F0.wireOp",EDGE,"E1")}),1.0]])]});
            extrude(context, id + "F6", {"entities" : qUnion([Q0]), "operationType" : NewBodyOperationType.ADD, "depth" : 16 * mm});
        }
        {
            var Q0;
            Q0=sQuery(id+"F0.wireOp",VERTEX,"E0.center");
            var Q1;
            Q1=makeQuery(id+"F1.opExtrude","SWEPT_BODY",BODY,{"disambiguationData":[OSD([sQuery(id+"F0.wireOp",EDGE,"E1"),sQuery(id+"F0.wireOp",EDGE,"E2"),sQuery(id+"F0.wireOp",EDGE,"E3"),sQuery(id+"F0.wireOp",EDGE,"E6.MirrorCS"),sQuery(id+"F0.wireOp",EDGE,"E7.MirrorCS"),sQuery(id+"F0.wireOp",EDGE,"E8.1.2"),sQuery(id+"F0.wireOp",EDGE,"E8.1.3"),sQuery(id+"F0.wireOp",EDGE,"E8.1.4"),sQuery(id+"F0.wireOp",EDGE,"E8.1.5"),sQuery(id+"F0.wireOp",EDGE,"E8.2.2"),sQuery(id+"F0.wireOp",EDGE,"E8.2.3"),sQuery(id+"F0.wireOp",EDGE,"E8.2.4"),sQuery(id+"F0.wireOp",EDGE,"E8.2.5"),sQuery(id+"F0.wireOp",EDGE,"E8.3.2"),sQuery(id+"F0.wireOp",EDGE,"E8.3.3"),sQuery(id+"F0.wireOp",EDGE,"E8.3.4"),sQuery(id+"F0.wireOp",EDGE,"E8.3.5"),sQuery(id+"F0.wireOp",EDGE,"E8.4.2"),sQuery(id+"F0.wireOp",EDGE,"E8.4.3"),sQuery(id+"F0.wireOp",EDGE,"E8.4.4"),sQuery(id+"F0.wireOp",EDGE,"E8.4.5"),sQuery(id+"F0.wireOp",EDGE,"E8.5.2"),sQuery(id+"F0.wireOp",EDGE,"E8.5.3"),sQuery(id+"F0.wireOp",EDGE,"E8.5.4"),sQuery(id+"F0.wireOp",EDGE,"E8.5.5"),sQuery(id+"F0.wireOp",EDGE,"E8.6.2"),sQuery(id+"F0.wireOp",EDGE,"E8.6.3"),sQuery(id+"F0.wireOp",EDGE,"E8.6.4"),sQuery(id+"F0.wireOp",EDGE,"E8.6.5"),sQuery(id+"F0.wireOp",EDGE,"E8.7.2"),sQuery(id+"F0.wireOp",EDGE,"E8.7.3"),sQuery(id+"F0.wireOp",EDGE,"E8.7.4"),sQuery(id+"F0.wireOp",EDGE,"E8.7.5"),sQuery(id+"F0.wireOp",EDGE,"E8.8.2"),sQuery(id+"F0.wireOp",EDGE,"E8.8.3"),sQuery(id+"F0.wireOp",EDGE,"E8.8.4"),sQuery(id+"F0.wireOp",EDGE,"E8.8.5"),sQuery(id+"F0.wireOp",EDGE,"E8.9.2"),sQuery(id+"F0.wireOp",EDGE,"E8.9.3"),sQuery(id+"F0.wireOp",EDGE,"E8.9.4"),sQuery(id+"F0.wireOp",EDGE,"E8.9.5"),sQuery(id+"F0.wireOp",EDGE,"E8.10.2"),sQuery(id+"F0.wireOp",EDGE,"E8.10.3"),sQuery(id+"F0.wireOp",EDGE,"E8.10.4"),sQuery(id+"F0.wireOp",EDGE,"E8.10.5"),sQuery(id+"F0.wireOp",EDGE,"E8.11.2"),sQuery(id+"F0.wireOp",EDGE,"E8.11.3"),sQuery(id+"F0.wireOp",EDGE,"E8.11.4"),sQuery(id+"F0.wireOp",EDGE,"E8.11.5"),sQuery(id+"F0.wireOp",EDGE,"E8.12.2"),sQuery(id+"F0.wireOp",EDGE,"E8.12.3"),sQuery(id+"F0.wireOp",EDGE,"E8.12.4"),sQuery(id+"F0.wireOp",EDGE,"E8.12.5"),sQuery(id+"F0.wireOp",EDGE,"E8.13.2"),sQuery(id+"F0.wireOp",EDGE,"E8.13.3"),sQuery(id+"F0.wireOp",EDGE,"E8.13.4"),sQuery(id+"F0.wireOp",EDGE,"E8.13.5"),sQuery(id+"F0.wireOp",EDGE,"E8.14.2"),sQuery(id+"F0.wireOp",EDGE,"E8.14.3"),sQuery(id+"F0.wireOp",EDGE,"E8.14.4"),sQuery(id+"F0.wireOp",EDGE,"E8.14.5"),sQuery(id+"F0.wireOp",EDGE,"E8.15.2"),sQuery(id+"F0.wireOp",EDGE,"E8.15.3"),sQuery(id+"F0.wireOp",EDGE,"E8.15.4"),sQuery(id+"F0.wireOp",EDGE,"E8.15.5"),sQuery(id+"F0.wireOp",EDGE,"E8.16.2"),sQuery(id+"F0.wireOp",EDGE,"E8.16.3"),sQuery(id+"F0.wireOp",EDGE,"E8.16.4"),sQuery(id+"F0.wireOp",EDGE,"E8.16.5"),sQuery(id+"F0.wireOp",EDGE,"E8.17.2"),sQuery(id+"F0.wireOp",EDGE,"E8.17.3"),sQuery(id+"F0.wireOp",EDGE,"E8.17.4"),sQuery(id+"F0.wireOp",EDGE,"E8.17.5"),sQuery(id+"F0.wireOp",EDGE,"E8.18.2"),sQuery(id+"F0.wireOp",EDGE,"E8.18.3"),sQuery(id+"F0.wireOp",EDGE,"E8.18.4"),sQuery(id+"F0.wireOp",EDGE,"E8.18.5"),sQuery(id+"F0.wireOp",EDGE,"E8.19.2"),sQuery(id+"F0.wireOp",EDGE,"E8.19.3"),sQuery(id+"F0.wireOp",EDGE,"E8.19.4"),sQuery(id+"F0.wireOp",EDGE,"E8.19.5"),sQuery(id+"F0.wireOp",EDGE,"E8.20.2"),sQuery(id+"F0.wireOp",EDGE,"E8.20.3"),sQuery(id+"F0.wireOp",EDGE,"E8.20.4"),sQuery(id+"F0.wireOp",EDGE,"E8.20.5"),sQuery(id+"F0.wireOp",EDGE,"E8.21.2"),sQuery(id+"F0.wireOp",EDGE,"E8.21.3"),sQuery(id+"F0.wireOp",EDGE,"E8.21.4"),sQuery(id+"F0.wireOp",EDGE,"E8.21.5"),sQuery(id+"F0.wireOp",EDGE,"E8.22.2"),sQuery(id+"F0.wireOp",EDGE,"E8.22.3"),sQuery(id+"F0.wireOp",EDGE,"E8.22.4"),sQuery(id+"F0.wireOp",EDGE,"E8.22.5"),sQuery(id+"F0.wireOp",EDGE,"E8.23.2"),sQuery(id+"F0.wireOp",EDGE,"E8.23.3"),sQuery(id+"F0.wireOp",EDGE,"E8.23.4"),sQuery(id+"F0.wireOp",EDGE,"E8.23.5"),sQuery(id+"F0.wireOp",EDGE,"E9"),sQuery(id+"F0.wireOp",EDGE,"E10.1.0"),sQuery(id+"F0.wireOp",EDGE,"E10.2.0"),sQuery(id+"F0.wireOp",EDGE,"E10.3.0"),sQuery(id+"F0.wireOp",EDGE,"E10.4.0"),sQuery(id+"F0.wireOp",EDGE,"E10.5.0"),sQuery(id+"F0.wireOp",EDGE,"E10.6.0"),sQuery(id+"F0.wireOp",EDGE,"E10.7.0"),sQuery(id+"F0.wireOp",EDGE,"E10.8.0"),sQuery(id+"F0.wireOp",EDGE,"E10.9.0"),sQuery(id+"F0.wireOp",EDGE,"E10.10.0"),sQuery(id+"F0.wireOp",EDGE,"E10.11.0"),sQuery(id+"F0.wireOp",EDGE,"E10.12.0"),sQuery(id+"F0.wireOp",EDGE,"E10.13.0"),sQuery(id+"F0.wireOp",EDGE,"E10.14.0"),sQuery(id+"F0.wireOp",EDGE,"E10.15.0"),sQuery(id+"F0.wireOp",EDGE,"E10.16.0"),sQuery(id+"F0.wireOp",EDGE,"E10.17.0"),sQuery(id+"F0.wireOp",EDGE,"E10.18.0"),sQuery(id+"F0.wireOp",EDGE,"E10.19.0"),sQuery(id+"F0.wireOp",EDGE,"E10.20.0"),sQuery(id+"F0.wireOp",EDGE,"E10.21.0"),sQuery(id+"F0.wireOp",EDGE,"E10.22.0"),sQuery(id+"F0.wireOp",EDGE,"E10.23.0")])]});
            hole(context, id + "F7", {"style" : HoleStyle.SIMPLE, "endStyle" : HoleEndStyle.THROUGH, "oppositeDirection" : true, "holeDiameter" : 6 * mm, "isTappedThrough" : true, "tappedDepth" : 12 * mm, "tapClearance" : 3, "locations" : qUnion([Q0]), "scope" : qUnion([Q1])});
        }
        {
            var Q0;
            Q0=makeQuery(id+"F4.opExtrude","CAP_EDGE",EDGE,{"disambiguationData":[OSD([sQuery(id+"F2.wireOp",EDGE,"E13")])],"isStart":true});
            var Q1;
            Q1=makeQuery(id+"F4.opExtrude","CAP_EDGE",EDGE,{"disambiguationData":[OSD([sQuery(id+"F2.wireOp",EDGE,"E13")])],"isStart":false});
            var Q2;
            Q2=makeQuery(id+"F5.opExtrude","CAP_EDGE",EDGE,{"disambiguationData":[OSD([sQuery(id+"F3.wireOp",EDGE,"E14")])],"isStart":false});
            var Q3;
            Q3=makeQuery(id+"F5.opExtrude","CAP_EDGE",EDGE,{"disambiguationData":[OSD([sQuery(id+"F3.wireOp",EDGE,"E14")])],"isStart":true});
            chamfer(context, id + "F8", {"entities" : qUnion([Q0, Q1, Q2, Q3]), "width" : 0.2 * mm, "tangentPropagation" : true});
        }
        {
            var Q0;
            Q0=makeQuery(id+"F6.opExtrude","CAP_EDGE",EDGE,{"disambiguationData":[OSD([sQuery(id+"F0.wireOp",EDGE,"E1")])],"isStart":false});
            var Q1;
            Q1=makeQuery(id+"F7.hole-0.boolean.opBoolean","INTERSECT",EDGE,{"derivedFrom":[makeQuery(id+"F6.opExtrude","CAP_FACE",FACE,{"disambiguationData":[OSD([sQuery(id+"F0.wireOp",EDGE,"E1")])],"isStart":false}),makeQuery(id+"F7.hole-0.opRevolve","SWEPT_FACE",FACE,{"disambiguationData":[OSD([sQuery(id+"F7.hole-0.sketch.wireOp",EDGE,"core_line_2")])]})]});
            var Q2;
            Q2=makeQuery(id+"F7.hole-0.boolean.opBoolean","COPY",EDGE,{"derivedFrom":makeQuery(id+"F7.hole-0.opRevolve","SWEPT_EDGE",EDGE,{"disambiguationData":[OSD([sQuery(id+"F7.hole-0.sketch.wireOp",EDGE,"core_line_2"),sQuery(id+"F7.hole-0.sketch.wireOp",EDGE,"core_line_3")])]})});
            chamfer(context, id + "F9", {"entities" : qUnion([Q0, Q1, Q2]), "width" : 0.5 * mm, "tangentPropagation" : true});
        }
    });
